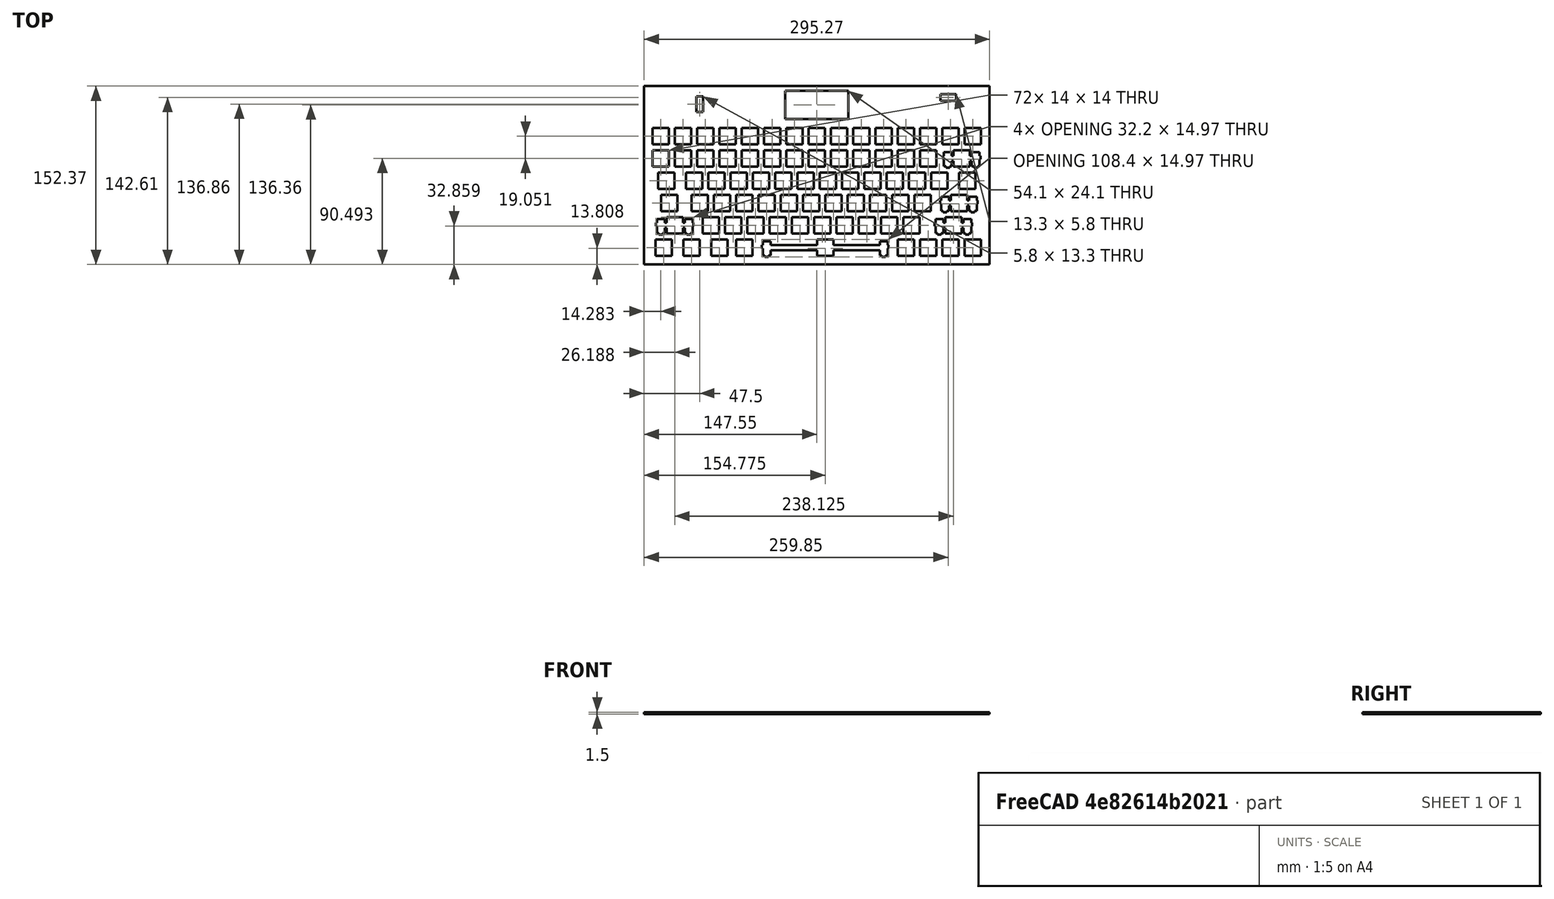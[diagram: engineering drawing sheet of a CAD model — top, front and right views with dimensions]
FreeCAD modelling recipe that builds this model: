
FCSTD DOCUMENT  (FreeCAD 0.21R33771 (Git))
Label: design
License: All rights reserved
LicenseURL: https://en.wikipedia.org/wiki/All_rights_reserved
objects: PartDesign::Body×2, Sketcher::SketchObject×1, PartDesign::Pad×1
note: 5 computed .brp shape members not serialized (recipe doc carries the construction recipe); baked Part::Feature solids carry a one-line shape summary decoded from their .brp

FEATURE [Sketcher::SketchObject] Sketch
  FullyConstrained = false
  MapMode = 5
  Support = -> [XY_Plane]
  sketch-geometry (484):
    g0: LineSegment StartX=55.0072 StartY=78.7329 StartZ=0 EndX=69.0079 EndY=78.7329 EndZ=0
    g1: LineSegment StartX=69.0079 StartY=78.7329 StartZ=0 EndX=69.0079 EndY=64.7333 EndZ=0
    g2: LineSegment StartX=69.0079 StartY=64.7333 StartZ=0 EndX=55.0072 EndY=64.7333 EndZ=0
    g3: LineSegment StartX=55.0072 StartY=64.7333 StartZ=0 EndX=55.0072 EndY=78.7329 EndZ=0
    g4: LineSegment StartX=64.5322 StartY=116.834 StartZ=0 EndX=78.5329 EndY=116.834 EndZ=0
    g5: LineSegment StartX=78.5329 StartY=116.834 StartZ=0 EndX=78.5329 EndY=102.835 EndZ=0
    g6: LineSegment StartX=78.5329 StartY=102.835 StartZ=0 EndX=64.5322 EndY=102.835 EndZ=0
    g7: LineSegment StartX=64.5322 StartY=102.835 StartZ=0 EndX=64.5322 EndY=116.834 EndZ=0
    g8: LineSegment StartX=0.0950846 StartY=152.658 StartZ=0 EndX=295.371 EndY=152.658 EndZ=0
    g9: LineSegment StartX=295.371 StartY=152.658 StartZ=0 EndX=295.371 EndY=0.2949 EndZ=0
    g10: LineSegment StartX=295.371 StartY=0.2949 StartZ=0 EndX=0.0950846 EndY=0.2949 EndZ=0
    g11: LineSegment StartX=0.0950846 StartY=0.2949 StartZ=0 EndX=0.0950846 EndY=152.658 EndZ=0
    g12: LineSegment StartX=147.876 StartY=21.5828 StartZ=0 EndX=147.876 EndY=16.8837 EndZ=0
    g13: LineSegment StartX=147.876 StartY=16.8837 StartZ=0 EndX=108.251 EndY=16.8837 EndZ=0
    g14: LineSegment StartX=108.251 StartY=16.8837 StartZ=0 EndX=108.251 EndY=20.1138 EndZ=0
    g15: LineSegment StartX=108.251 StartY=20.1138 StartZ=0 EndX=101.501 EndY=20.1138 EndZ=0
    g16: LineSegment StartX=101.501 StartY=20.1138 StartZ=0 EndX=101.501 EndY=16.8837 EndZ=0
    g17: LineSegment StartX=101.501 StartY=16.8837 StartZ=0 EndX=100.675 EndY=16.8837 EndZ=0
    g18: LineSegment StartX=100.675 StartY=16.8837 StartZ=0 EndX=100.675 EndY=14.0836 EndZ=0
    g19: LineSegment StartX=100.675 StartY=14.0836 StartZ=0 EndX=101.501 EndY=14.0836 EndZ=0
    g20: LineSegment StartX=101.501 StartY=14.0836 StartZ=0 EndX=101.501 EndY=7.81346 EndZ=0
    g21: LineSegment StartX=101.501 StartY=7.81346 StartZ=0 EndX=103.226 EndY=7.81346 EndZ=0
    g22: LineSegment StartX=103.226 StartY=7.81346 StartZ=0 EndX=103.226 EndY=6.61321 EndZ=0
    g23: LineSegment StartX=103.226 StartY=6.61321 StartZ=0 EndX=106.525 EndY=6.61321 EndZ=0
    g24: LineSegment StartX=106.525 StartY=6.61321 StartZ=0 EndX=106.525 EndY=7.81346 EndZ=0
    g25: LineSegment StartX=106.525 StartY=7.81346 StartZ=0 EndX=108.251 EndY=7.81346 EndZ=0
    g26: LineSegment StartX=108.251 StartY=7.81346 StartZ=0 EndX=108.251 EndY=12.2838 EndZ=0
    g27: LineSegment StartX=108.251 StartY=12.2838 StartZ=0 EndX=147.876 EndY=12.2838 EndZ=0
    g28: LineSegment StartX=147.876 StartY=12.2838 StartZ=0 EndX=147.876 EndY=7.58335 EndZ=0
    g29: LineSegment StartX=147.876 StartY=7.58335 StartZ=0 EndX=161.875 EndY=7.58335 EndZ=0
    g30: LineSegment StartX=161.875 StartY=7.58335 StartZ=0 EndX=161.875 EndY=12.2838 EndZ=0
    g31: LineSegment StartX=161.875 StartY=12.2838 StartZ=0 EndX=201.501 EndY=12.2838 EndZ=0
    g32: LineSegment StartX=201.501 StartY=12.2838 StartZ=0 EndX=201.501 EndY=7.81346 EndZ=0
    g33: LineSegment StartX=201.501 StartY=7.81346 StartZ=0 EndX=203.225 EndY=7.81346 EndZ=0
    g34: LineSegment StartX=203.225 StartY=7.81346 StartZ=0 EndX=203.225 EndY=6.61321 EndZ=0
    g35: LineSegment StartX=203.225 StartY=6.61321 StartZ=0 EndX=206.525 EndY=6.61321 EndZ=0
    g36: LineSegment StartX=206.525 StartY=6.61321 StartZ=0 EndX=206.525 EndY=7.81346 EndZ=0
    g37: LineSegment StartX=206.525 StartY=7.81346 StartZ=0 EndX=208.25 EndY=7.81346 EndZ=0
    g38: LineSegment StartX=208.25 StartY=7.81346 StartZ=0 EndX=208.25 EndY=14.0836 EndZ=0
    g39: LineSegment StartX=208.25 StartY=14.0836 StartZ=0 EndX=209.076 EndY=14.0836 EndZ=0
    g40: LineSegment StartX=209.076 StartY=14.0836 StartZ=0 EndX=209.076 EndY=16.8837 EndZ=0
    g41: LineSegment StartX=209.076 StartY=16.8837 StartZ=0 EndX=208.25 EndY=16.8837 EndZ=0
    g42: LineSegment StartX=208.25 StartY=16.8837 StartZ=0 EndX=208.25 EndY=20.1138 EndZ=0
    g43: LineSegment StartX=208.25 StartY=20.1138 StartZ=0 EndX=201.501 EndY=20.1138 EndZ=0
    g44: LineSegment StartX=201.501 StartY=20.1138 StartZ=0 EndX=201.501 EndY=16.8837 EndZ=0
    g45: LineSegment StartX=201.501 StartY=16.8837 StartZ=0 EndX=161.875 EndY=16.8837 EndZ=0
    g46: LineSegment StartX=161.875 StartY=16.8837 StartZ=0 EndX=161.875 EndY=21.5828 EndZ=0
    g47: LineSegment StartX=161.875 StartY=21.5828 StartZ=0 EndX=147.876 EndY=21.5828 EndZ=0
    g48: LineSegment StartX=9.76341 StartY=21.5828 StartZ=0 EndX=23.7629 EndY=21.5828 EndZ=0
    g49: LineSegment StartX=23.7629 StartY=21.5828 StartZ=0 EndX=23.7629 EndY=7.58335 EndZ=0
    g50: LineSegment StartX=23.7629 StartY=7.58335 StartZ=0 EndX=9.76341 EndY=7.58335 EndZ=0
    g51: LineSegment StartX=9.76341 StartY=7.58335 StartZ=0 EndX=9.76341 EndY=21.5828 EndZ=0
    g52: LineSegment StartX=33.5759 StartY=21.5828 StartZ=0 EndX=47.5753 EndY=21.5828 EndZ=0
    g53: LineSegment StartX=47.5753 StartY=21.5828 StartZ=0 EndX=47.5753 EndY=7.58335 EndZ=0
    g54: LineSegment StartX=47.5753 StartY=7.58335 StartZ=0 EndX=33.5759 EndY=7.58335 EndZ=0
    g55: LineSegment StartX=33.5759 StartY=7.58335 StartZ=0 EndX=33.5759 EndY=21.5828 EndZ=0
    g56: LineSegment StartX=57.3885 StartY=21.5828 StartZ=0 EndX=71.3878 EndY=21.5828 EndZ=0
    g57: LineSegment StartX=71.3878 StartY=21.5828 StartZ=0 EndX=71.3878 EndY=7.58335 EndZ=0
    g58: LineSegment StartX=71.3878 StartY=7.58335 StartZ=0 EndX=57.3885 EndY=7.58335 EndZ=0
    g59: LineSegment StartX=57.3885 StartY=7.58335 StartZ=0 EndX=57.3885 EndY=21.5828 EndZ=0
    g60: LineSegment StartX=78.8197 StartY=21.5828 StartZ=0 EndX=92.819 EndY=21.5828 EndZ=0
    g61: LineSegment StartX=92.819 StartY=21.5828 StartZ=0 EndX=92.819 EndY=7.58335 EndZ=0
    g62: LineSegment StartX=92.819 StartY=7.58335 StartZ=0 EndX=78.8197 EndY=7.58335 EndZ=0
    g63: LineSegment StartX=78.8197 StartY=7.58335 StartZ=0 EndX=78.8197 EndY=21.5828 EndZ=0
    g64: LineSegment StartX=216.932 StartY=21.5828 StartZ=0 EndX=230.933 EndY=21.5828 EndZ=0
    g65: LineSegment StartX=230.933 StartY=21.5828 StartZ=0 EndX=230.933 EndY=7.58335 EndZ=0
    g66: LineSegment StartX=230.933 StartY=7.58335 StartZ=0 EndX=216.932 EndY=7.58335 EndZ=0
    g67: LineSegment StartX=216.932 StartY=7.58335 StartZ=0 EndX=216.932 EndY=21.5828 EndZ=0
    g68: LineSegment StartX=235.982 StartY=21.5828 StartZ=0 EndX=249.983 EndY=21.5828 EndZ=0
    g69: LineSegment StartX=249.983 StartY=21.5828 StartZ=0 EndX=249.983 EndY=7.58335 EndZ=0
    g70: LineSegment StartX=249.983 StartY=7.58335 StartZ=0 EndX=235.982 EndY=7.58335 EndZ=0
    g71: LineSegment StartX=235.982 StartY=7.58335 StartZ=0 EndX=235.982 EndY=21.5828 EndZ=0
    g72: LineSegment StartX=255.032 StartY=21.5828 StartZ=0 EndX=269.033 EndY=21.5828 EndZ=0
    g73: LineSegment StartX=269.033 StartY=21.5828 StartZ=0 EndX=269.033 EndY=7.58335 EndZ=0
    g74: LineSegment StartX=269.033 StartY=7.58335 StartZ=0 EndX=255.032 EndY=7.58335 EndZ=0
    g75: LineSegment StartX=255.032 StartY=7.58335 StartZ=0 EndX=255.032 EndY=21.5828 EndZ=0
    g76: LineSegment StartX=274.082 StartY=21.5828 StartZ=0 EndX=288.083 EndY=21.5828 EndZ=0
    g77: LineSegment StartX=288.083 StartY=21.5828 StartZ=0 EndX=288.083 EndY=7.58335 EndZ=0
    g78: LineSegment StartX=288.083 StartY=7.58335 StartZ=0 EndX=274.082 EndY=7.58335 EndZ=0
    g79: LineSegment StartX=274.082 StartY=7.58335 StartZ=0 EndX=274.082 EndY=21.5828 EndZ=0
    g80: LineSegment StartX=19.2884 StartY=40.6344 StartZ=0 EndX=19.2884 EndY=35.9336 EndZ=0
    g81: LineSegment StartX=19.2884 StartY=35.9336 StartZ=0 EndX=17.7629 EndY=35.9336 EndZ=0
    g82: LineSegment StartX=17.7629 StartY=35.9336 StartZ=0 EndX=17.7629 EndY=39.164 EndZ=0
    g83: LineSegment StartX=17.7629 StartY=39.164 StartZ=0 EndX=11.0133 EndY=39.164 EndZ=0
    g84: LineSegment StartX=11.0133 StartY=39.164 StartZ=0 EndX=11.0133 EndY=35.9336 EndZ=0
    g85: LineSegment StartX=11.0133 StartY=35.9336 StartZ=0 EndX=10.1878 EndY=35.9336 EndZ=0
    g86: LineSegment StartX=10.1878 StartY=35.9336 StartZ=0 EndX=10.1878 EndY=33.1349 EndZ=0
    g87: LineSegment StartX=10.1878 StartY=33.1349 StartZ=0 EndX=11.0133 EndY=33.1349 EndZ=0
    g88: LineSegment StartX=11.0133 StartY=33.1349 StartZ=0 EndX=11.0133 EndY=26.8648 EndZ=0
    g89: LineSegment StartX=11.0133 StartY=26.8648 StartZ=0 EndX=12.7386 EndY=26.8648 EndZ=0
    g90: LineSegment StartX=12.7386 StartY=26.8648 StartZ=0 EndX=12.7386 EndY=25.6632 EndZ=0
    g91: LineSegment StartX=12.7386 StartY=25.6632 StartZ=0 EndX=16.039 EndY=25.6632 EndZ=0
    g92: LineSegment StartX=16.039 StartY=25.6632 StartZ=0 EndX=16.039 EndY=26.8648 EndZ=0
    g93: LineSegment StartX=16.039 StartY=26.8648 StartZ=0 EndX=17.7629 EndY=26.8648 EndZ=0
    g94: LineSegment StartX=17.7629 StartY=26.8648 StartZ=0 EndX=17.7629 EndY=31.3338 EndZ=0
    g95: LineSegment StartX=17.7629 StartY=31.3338 StartZ=0 EndX=19.2884 EndY=31.3338 EndZ=0
    g96: LineSegment StartX=19.2884 StartY=31.3338 StartZ=0 EndX=19.2884 EndY=26.6347 EndZ=0
    g97: LineSegment StartX=19.2884 StartY=26.6347 StartZ=0 EndX=33.2879 EndY=26.6347 EndZ=0
    g98: LineSegment StartX=33.2879 StartY=26.6347 StartZ=0 EndX=33.2879 EndY=31.3338 EndZ=0
    g99: LineSegment StartX=33.2879 StartY=31.3338 StartZ=0 EndX=34.8134 EndY=31.3338 EndZ=0
    g100: LineSegment StartX=34.8134 StartY=31.3338 StartZ=0 EndX=34.8134 EndY=26.8648 EndZ=0
    g101: LineSegment StartX=34.8134 StartY=26.8648 StartZ=0 EndX=36.5386 EndY=26.8648 EndZ=0
    g102: LineSegment StartX=36.5386 StartY=26.8648 StartZ=0 EndX=36.5386 EndY=25.6632 EndZ=0
    g103: LineSegment StartX=36.5386 StartY=25.6632 StartZ=0 EndX=39.8392 EndY=25.6632 EndZ=0
    g104: LineSegment StartX=39.8392 StartY=25.6632 StartZ=0 EndX=39.8392 EndY=26.8648 EndZ=0
    g105: LineSegment StartX=39.8392 StartY=26.8648 StartZ=0 EndX=41.5629 EndY=26.8648 EndZ=0
    g106: LineSegment StartX=41.5629 StartY=26.8648 StartZ=0 EndX=41.5629 EndY=33.1349 EndZ=0
    g107: LineSegment StartX=41.5629 StartY=33.1349 StartZ=0 EndX=42.3884 EndY=33.1349 EndZ=0
    g108: LineSegment StartX=42.3884 StartY=33.1349 StartZ=0 EndX=42.3884 EndY=35.9336 EndZ=0
    g109: LineSegment StartX=42.3884 StartY=35.9336 StartZ=0 EndX=41.5629 EndY=35.9336 EndZ=0
    g110: LineSegment StartX=41.5629 StartY=35.9336 StartZ=0 EndX=41.5629 EndY=39.164 EndZ=0
    g111: LineSegment StartX=41.5629 StartY=39.164 StartZ=0 EndX=34.8134 EndY=39.164 EndZ=0
    g112: LineSegment StartX=34.8134 StartY=39.164 StartZ=0 EndX=34.8134 EndY=35.9336 EndZ=0
    g113: LineSegment StartX=34.8134 StartY=35.9336 StartZ=0 EndX=33.2879 EndY=35.9336 EndZ=0
    g114: LineSegment StartX=33.2879 StartY=35.9336 StartZ=0 EndX=33.2879 EndY=40.6344 EndZ=0
    g115: LineSegment StartX=33.2879 StartY=40.6344 StartZ=0 EndX=19.2884 EndY=40.6344 EndZ=0
    g116: LineSegment StartX=257.413 StartY=40.6344 StartZ=0 EndX=257.413 EndY=35.9336 EndZ=0
    g117: LineSegment StartX=257.413 StartY=35.9336 StartZ=0 EndX=255.888 EndY=35.9336 EndZ=0
    g118: LineSegment StartX=255.888 StartY=35.9336 StartZ=0 EndX=255.888 EndY=39.164 EndZ=0
    g119: LineSegment StartX=255.888 StartY=39.164 StartZ=0 EndX=249.138 EndY=39.164 EndZ=0
    g120: LineSegment StartX=249.138 StartY=39.164 StartZ=0 EndX=249.138 EndY=35.9336 EndZ=0
    g121: LineSegment StartX=249.138 StartY=35.9336 StartZ=0 EndX=248.313 EndY=35.9336 EndZ=0
    g122: LineSegment StartX=248.313 StartY=35.9336 StartZ=0 EndX=248.313 EndY=33.1349 EndZ=0
    g123: LineSegment StartX=248.313 StartY=33.1349 StartZ=0 EndX=249.138 EndY=33.1349 EndZ=0
    g124: LineSegment StartX=249.138 StartY=33.1349 StartZ=0 EndX=249.138 EndY=26.8648 EndZ=0
    g125: LineSegment StartX=249.138 StartY=26.8648 StartZ=0 EndX=250.863 EndY=26.8648 EndZ=0
    g126: LineSegment StartX=250.863 StartY=26.8648 StartZ=0 EndX=250.863 EndY=25.6632 EndZ=0
    g127: LineSegment StartX=250.863 StartY=25.6632 StartZ=0 EndX=254.164 EndY=25.6632 EndZ=0
    g128: LineSegment StartX=254.164 StartY=25.6632 StartZ=0 EndX=254.164 EndY=26.8648 EndZ=0
    g129: LineSegment StartX=254.164 StartY=26.8648 StartZ=0 EndX=255.888 EndY=26.8648 EndZ=0
    g130: LineSegment StartX=255.888 StartY=26.8648 StartZ=0 EndX=255.888 EndY=31.3338 EndZ=0
    g131: LineSegment StartX=255.888 StartY=31.3338 StartZ=0 EndX=257.413 EndY=31.3338 EndZ=0
    g132: LineSegment StartX=257.413 StartY=31.3338 StartZ=0 EndX=257.413 EndY=26.6347 EndZ=0
    g133: LineSegment StartX=257.413 StartY=26.6347 StartZ=0 EndX=271.413 EndY=26.6347 EndZ=0
    g134: LineSegment StartX=271.413 StartY=26.6347 StartZ=0 EndX=271.413 EndY=31.3338 EndZ=0
    g135: LineSegment StartX=271.413 StartY=31.3338 StartZ=0 EndX=272.939 EndY=31.3338 EndZ=0
    g136: LineSegment StartX=272.939 StartY=31.3338 StartZ=0 EndX=272.939 EndY=26.8648 EndZ=0
    g137: LineSegment StartX=272.939 StartY=26.8648 StartZ=0 EndX=274.664 EndY=26.8648 EndZ=0
    g138: LineSegment StartX=274.664 StartY=26.8648 StartZ=0 EndX=274.664 EndY=25.6632 EndZ=0
    g139: LineSegment StartX=274.664 StartY=25.6632 StartZ=0 EndX=277.964 EndY=25.6632 EndZ=0
    g140: LineSegment StartX=277.964 StartY=25.6632 StartZ=0 EndX=277.964 EndY=26.8648 EndZ=0
    g141: LineSegment StartX=277.964 StartY=26.8648 StartZ=0 EndX=279.688 EndY=26.8648 EndZ=0
    g142: LineSegment StartX=279.688 StartY=26.8648 StartZ=0 EndX=279.688 EndY=33.1349 EndZ=0
    g143: LineSegment StartX=279.688 StartY=33.1349 StartZ=0 EndX=280.513 EndY=33.1349 EndZ=0
    g144: LineSegment StartX=280.513 StartY=33.1349 StartZ=0 EndX=280.513 EndY=35.9336 EndZ=0
    g145: LineSegment StartX=280.513 StartY=35.9336 StartZ=0 EndX=279.688 EndY=35.9336 EndZ=0
    g146: LineSegment StartX=279.688 StartY=35.9336 StartZ=0 EndX=279.688 EndY=39.164 EndZ=0
    g147: LineSegment StartX=279.688 StartY=39.164 StartZ=0 EndX=272.939 EndY=39.164 EndZ=0
    g148: LineSegment StartX=272.939 StartY=39.164 StartZ=0 EndX=272.939 EndY=35.9336 EndZ=0
    g149: LineSegment StartX=272.939 StartY=35.9336 StartZ=0 EndX=271.413 EndY=35.9336 EndZ=0
    g150: LineSegment StartX=271.413 StartY=35.9336 StartZ=0 EndX=271.413 EndY=40.6344 EndZ=0
    g151: LineSegment StartX=271.413 StartY=40.6344 StartZ=0 EndX=257.413 EndY=40.6344 EndZ=0
    g152: LineSegment StartX=50.2447 StartY=40.6344 StartZ=0 EndX=64.244 EndY=40.6344 EndZ=0
    g153: LineSegment StartX=64.244 StartY=40.6344 StartZ=0 EndX=64.244 EndY=26.6347 EndZ=0
    g154: LineSegment StartX=64.244 StartY=26.6347 StartZ=0 EndX=50.2447 EndY=26.6347 EndZ=0
    g155: LineSegment StartX=50.2447 StartY=26.6347 StartZ=0 EndX=50.2447 EndY=40.6344 EndZ=0
    g156: LineSegment StartX=69.2947 StartY=40.6344 StartZ=0 EndX=83.294 EndY=40.6344 EndZ=0
    g157: LineSegment StartX=83.294 StartY=40.6344 StartZ=0 EndX=83.294 EndY=26.6347 EndZ=0
    g158: LineSegment StartX=83.294 StartY=26.6347 StartZ=0 EndX=69.2947 EndY=26.6347 EndZ=0
    g159: LineSegment StartX=69.2947 StartY=26.6347 StartZ=0 EndX=69.2947 EndY=40.6344 EndZ=0
    g160: LineSegment StartX=88.3447 StartY=40.6344 StartZ=0 EndX=102.344 EndY=40.6344 EndZ=0
    g161: LineSegment StartX=102.344 StartY=40.6344 StartZ=0 EndX=102.344 EndY=26.6347 EndZ=0
    g162: LineSegment StartX=102.344 StartY=26.6347 StartZ=0 EndX=88.3447 EndY=26.6347 EndZ=0
    g163: LineSegment StartX=88.3447 StartY=26.6347 StartZ=0 EndX=88.3447 EndY=40.6344 EndZ=0
    g164: LineSegment StartX=107.395 StartY=40.6344 StartZ=0 EndX=121.394 EndY=40.6344 EndZ=0
    g165: LineSegment StartX=121.394 StartY=40.6344 StartZ=0 EndX=121.394 EndY=26.6347 EndZ=0
    g166: LineSegment StartX=121.394 StartY=26.6347 StartZ=0 EndX=107.395 EndY=26.6347 EndZ=0
    g167: LineSegment StartX=107.395 StartY=26.6347 StartZ=0 EndX=107.395 EndY=40.6344 EndZ=0
    g168: LineSegment StartX=126.445 StartY=40.6344 StartZ=0 EndX=140.444 EndY=40.6344 EndZ=0
    g169: LineSegment StartX=140.444 StartY=40.6344 StartZ=0 EndX=140.444 EndY=26.6347 EndZ=0
    g170: LineSegment StartX=140.444 StartY=26.6347 StartZ=0 EndX=126.445 EndY=26.6347 EndZ=0
    g171: LineSegment StartX=126.445 StartY=26.6347 StartZ=0 EndX=126.445 EndY=40.6344 EndZ=0
    g172: LineSegment StartX=145.495 StartY=40.6344 StartZ=0 EndX=159.494 EndY=40.6344 EndZ=0
    g173: LineSegment StartX=159.494 StartY=40.6344 StartZ=0 EndX=159.494 EndY=26.6347 EndZ=0
    g174: LineSegment StartX=159.494 StartY=26.6347 StartZ=0 EndX=145.495 EndY=26.6347 EndZ=0
    g175: LineSegment StartX=145.495 StartY=26.6347 StartZ=0 EndX=145.495 EndY=40.6344 EndZ=0
    g176: LineSegment StartX=164.545 StartY=40.6344 StartZ=0 EndX=178.544 EndY=40.6344 EndZ=0
    g177: LineSegment StartX=178.544 StartY=40.6344 StartZ=0 EndX=178.544 EndY=26.6347 EndZ=0
    g178: LineSegment StartX=178.544 StartY=26.6347 StartZ=0 EndX=164.545 EndY=26.6347 EndZ=0
    g179: LineSegment StartX=164.545 StartY=26.6347 StartZ=0 EndX=164.545 EndY=40.6344 EndZ=0
    g180: LineSegment StartX=183.595 StartY=40.6344 StartZ=0 EndX=197.594 EndY=40.6344 EndZ=0
    g181: LineSegment StartX=197.594 StartY=40.6344 StartZ=0 EndX=197.594 EndY=26.6347 EndZ=0
    g182: LineSegment StartX=197.594 StartY=26.6347 StartZ=0 EndX=183.595 EndY=26.6347 EndZ=0
    g183: LineSegment StartX=183.595 StartY=26.6347 StartZ=0 EndX=183.595 EndY=40.6344 EndZ=0
    g184: LineSegment StartX=202.645 StartY=40.6344 StartZ=0 EndX=216.644 EndY=40.6344 EndZ=0
    g185: LineSegment StartX=216.644 StartY=40.6344 StartZ=0 EndX=216.644 EndY=26.6347 EndZ=0
    g186: LineSegment StartX=216.644 StartY=26.6347 StartZ=0 EndX=202.645 EndY=26.6347 EndZ=0
    g187: LineSegment StartX=202.645 StartY=26.6347 StartZ=0 EndX=202.645 EndY=40.6344 EndZ=0
    g188: LineSegment StartX=221.695 StartY=40.6344 StartZ=0 EndX=235.694 EndY=40.6344 EndZ=0
    g189: LineSegment StartX=235.694 StartY=40.6344 StartZ=0 EndX=235.694 EndY=26.6347 EndZ=0
    g190: LineSegment StartX=235.694 StartY=26.6347 StartZ=0 EndX=221.695 EndY=26.6347 EndZ=0
    g191: LineSegment StartX=221.695 StartY=26.6347 StartZ=0 EndX=221.695 EndY=40.6344 EndZ=0
    g192: LineSegment StartX=262.176 StartY=59.6829 StartZ=0 EndX=262.176 EndY=54.9836 EndZ=0
    g193: LineSegment StartX=262.176 StartY=54.9836 StartZ=0 EndX=260.651 EndY=54.9836 EndZ=0
    g194: LineSegment StartX=260.651 StartY=54.9836 StartZ=0 EndX=260.651 EndY=58.214 EndZ=0
    g195: LineSegment StartX=260.651 StartY=58.214 StartZ=0 EndX=253.899 EndY=58.214 EndZ=0
    g196: LineSegment StartX=253.899 StartY=58.214 StartZ=0 EndX=253.899 EndY=54.9836 EndZ=0
    g197: LineSegment StartX=253.899 StartY=54.9836 StartZ=0 EndX=253.075 EndY=54.9836 EndZ=0
    g198: LineSegment StartX=253.075 StartY=54.9836 StartZ=0 EndX=253.075 EndY=52.1836 EndZ=0
    g199: LineSegment StartX=253.075 StartY=52.1836 StartZ=0 EndX=253.899 EndY=52.1836 EndZ=0
    g200: LineSegment StartX=253.899 StartY=52.1836 StartZ=0 EndX=253.899 EndY=45.9147 EndZ=0
    g201: LineSegment StartX=253.899 StartY=45.9147 StartZ=0 EndX=255.626 EndY=45.9147 EndZ=0
    g202: LineSegment StartX=255.626 StartY=45.9147 StartZ=0 EndX=255.626 EndY=44.7132 EndZ=0
    g203: LineSegment StartX=255.626 StartY=44.7132 StartZ=0 EndX=258.925 EndY=44.7132 EndZ=0
    g204: LineSegment StartX=258.925 StartY=44.7132 StartZ=0 EndX=258.925 EndY=45.9147 EndZ=0
    g205: LineSegment StartX=258.925 StartY=45.9147 StartZ=0 EndX=260.651 EndY=45.9147 EndZ=0
    g206: LineSegment StartX=260.651 StartY=45.9147 StartZ=0 EndX=260.651 EndY=50.3837 EndZ=0
    g207: LineSegment StartX=260.651 StartY=50.3837 StartZ=0 EndX=262.176 EndY=50.3837 EndZ=0
    g208: LineSegment StartX=262.176 StartY=50.3837 StartZ=0 EndX=262.176 EndY=45.6833 EndZ=0
    g209: LineSegment StartX=262.176 StartY=45.6833 StartZ=0 EndX=276.175 EndY=45.6833 EndZ=0
    g210: LineSegment StartX=276.175 StartY=45.6833 StartZ=0 EndX=276.175 EndY=50.3837 EndZ=0
    g211: LineSegment StartX=276.175 StartY=50.3837 StartZ=0 EndX=277.701 EndY=50.3837 EndZ=0
    g212: LineSegment StartX=277.701 StartY=50.3837 StartZ=0 EndX=277.701 EndY=45.9147 EndZ=0
    g213: LineSegment StartX=277.701 StartY=45.9147 StartZ=0 EndX=279.425 EndY=45.9147 EndZ=0
    g214: LineSegment StartX=279.425 StartY=45.9147 StartZ=0 EndX=279.425 EndY=44.7132 EndZ=0
    g215: LineSegment StartX=279.425 StartY=44.7132 StartZ=0 EndX=282.725 EndY=44.7132 EndZ=0
    g216: LineSegment StartX=282.725 StartY=44.7132 StartZ=0 EndX=282.725 EndY=45.9147 EndZ=0
    g217: LineSegment StartX=282.725 StartY=45.9147 StartZ=0 EndX=284.45 EndY=45.9147 EndZ=0
    g218: LineSegment StartX=284.45 StartY=45.9147 StartZ=0 EndX=284.45 EndY=52.1836 EndZ=0
    g219: LineSegment StartX=284.45 StartY=52.1836 StartZ=0 EndX=285.276 EndY=52.1836 EndZ=0
    g220: LineSegment StartX=285.276 StartY=52.1836 StartZ=0 EndX=285.276 EndY=54.9836 EndZ=0
    g221: LineSegment StartX=285.276 StartY=54.9836 StartZ=0 EndX=284.45 EndY=54.9836 EndZ=0
    g222: LineSegment StartX=284.45 StartY=54.9836 StartZ=0 EndX=284.45 EndY=58.214 EndZ=0
    g223: LineSegment StartX=284.45 StartY=58.214 StartZ=0 EndX=277.701 EndY=58.214 EndZ=0
    g224: LineSegment StartX=277.701 StartY=58.214 StartZ=0 EndX=277.701 EndY=54.9836 EndZ=0
    g225: LineSegment StartX=277.701 StartY=54.9836 StartZ=0 EndX=276.175 EndY=54.9836 EndZ=0
    g226: LineSegment StartX=276.175 StartY=54.9836 StartZ=0 EndX=276.175 EndY=59.6829 EndZ=0
    g227: LineSegment StartX=276.175 StartY=59.6829 StartZ=0 EndX=262.176 EndY=59.6829 EndZ=0
    g228: LineSegment StartX=14.5259 StartY=59.6829 StartZ=0 EndX=28.5254 EndY=59.6829 EndZ=0
    g229: LineSegment StartX=28.5254 StartY=59.6829 StartZ=0 EndX=28.5254 EndY=45.6833 EndZ=0
    g230: LineSegment StartX=28.5254 StartY=45.6833 StartZ=0 EndX=14.5259 EndY=45.6833 EndZ=0
    g231: LineSegment StartX=14.5259 StartY=45.6833 StartZ=0 EndX=14.5259 EndY=59.6829 EndZ=0
    g232: LineSegment StartX=40.7197 StartY=59.6829 StartZ=0 EndX=54.719 EndY=59.6829 EndZ=0
    g233: LineSegment StartX=54.719 StartY=59.6829 StartZ=0 EndX=54.719 EndY=45.6833 EndZ=0
    g234: LineSegment StartX=54.719 StartY=45.6833 StartZ=0 EndX=40.7197 EndY=45.6833 EndZ=0
    g235: LineSegment StartX=40.7197 StartY=45.6833 StartZ=0 EndX=40.7197 EndY=59.6829 EndZ=0
    g236: LineSegment StartX=59.7697 StartY=59.6829 StartZ=0 EndX=73.769 EndY=59.6829 EndZ=0
    g237: LineSegment StartX=73.769 StartY=59.6829 StartZ=0 EndX=73.769 EndY=45.6833 EndZ=0
    g238: LineSegment StartX=73.769 StartY=45.6833 StartZ=0 EndX=59.7697 EndY=45.6833 EndZ=0
    g239: LineSegment StartX=59.7697 StartY=45.6833 StartZ=0 EndX=59.7697 EndY=59.6829 EndZ=0
    g240: LineSegment StartX=78.8197 StartY=59.6829 StartZ=0 EndX=92.819 EndY=59.6829 EndZ=0
    g241: LineSegment StartX=92.819 StartY=59.6829 StartZ=0 EndX=92.819 EndY=45.6833 EndZ=0
    g242: LineSegment StartX=92.819 StartY=45.6833 StartZ=0 EndX=78.8197 EndY=45.6833 EndZ=0
    g243: LineSegment StartX=78.8197 StartY=45.6833 StartZ=0 EndX=78.8197 EndY=59.6829 EndZ=0
    g244: LineSegment StartX=97.8697 StartY=59.6829 StartZ=0 EndX=111.869 EndY=59.6829 EndZ=0
    g245: LineSegment StartX=111.869 StartY=59.6829 StartZ=0 EndX=111.869 EndY=45.6833 EndZ=0
    g246: LineSegment StartX=111.869 StartY=45.6833 StartZ=0 EndX=97.8697 EndY=45.6833 EndZ=0
    g247: LineSegment StartX=97.8697 StartY=45.6833 StartZ=0 EndX=97.8697 EndY=59.6829 EndZ=0
    g248: LineSegment StartX=116.92 StartY=59.6829 StartZ=0 EndX=130.919 EndY=59.6829 EndZ=0
    g249: LineSegment StartX=130.919 StartY=59.6829 StartZ=0 EndX=130.919 EndY=45.6833 EndZ=0
    g250: LineSegment StartX=130.919 StartY=45.6833 StartZ=0 EndX=116.92 EndY=45.6833 EndZ=0
    g251: LineSegment StartX=116.92 StartY=45.6833 StartZ=0 EndX=116.92 EndY=59.6829 EndZ=0
    g252: LineSegment StartX=135.97 StartY=59.6829 StartZ=0 EndX=149.969 EndY=59.6829 EndZ=0
    g253: LineSegment StartX=149.969 StartY=59.6829 StartZ=0 EndX=149.969 EndY=45.6833 EndZ=0
    g254: LineSegment StartX=149.969 StartY=45.6833 StartZ=0 EndX=135.97 EndY=45.6833 EndZ=0
    g255: LineSegment StartX=135.97 StartY=45.6833 StartZ=0 EndX=135.97 EndY=59.6829 EndZ=0
    g256: LineSegment StartX=155.02 StartY=59.6829 StartZ=0 EndX=169.019 EndY=59.6829 EndZ=0
    g257: LineSegment StartX=169.019 StartY=59.6829 StartZ=0 EndX=169.019 EndY=45.6833 EndZ=0
    g258: LineSegment StartX=169.019 StartY=45.6833 StartZ=0 EndX=155.02 EndY=45.6833 EndZ=0
    g259: LineSegment StartX=155.02 StartY=45.6833 StartZ=0 EndX=155.02 EndY=59.6829 EndZ=0
    g260: LineSegment StartX=174.07 StartY=59.6829 StartZ=0 EndX=188.069 EndY=59.6829 EndZ=0
    g261: LineSegment StartX=188.069 StartY=59.6829 StartZ=0 EndX=188.069 EndY=45.6833 EndZ=0
    g262: LineSegment StartX=188.069 StartY=45.6833 StartZ=0 EndX=174.07 EndY=45.6833 EndZ=0
    g263: LineSegment StartX=174.07 StartY=45.6833 StartZ=0 EndX=174.07 EndY=59.6829 EndZ=0
    g264: LineSegment StartX=193.12 StartY=59.6829 StartZ=0 EndX=207.119 EndY=59.6829 EndZ=0
    g265: LineSegment StartX=207.119 StartY=59.6829 StartZ=0 EndX=207.119 EndY=45.6833 EndZ=0
    g266: LineSegment StartX=207.119 StartY=45.6833 StartZ=0 EndX=193.12 EndY=45.6833 EndZ=0
    g267: LineSegment StartX=193.12 StartY=45.6833 StartZ=0 EndX=193.12 EndY=59.6829 EndZ=0
    g268: LineSegment StartX=212.17 StartY=59.6829 StartZ=0 EndX=226.169 EndY=59.6829 EndZ=0
    g269: LineSegment StartX=226.169 StartY=59.6829 StartZ=0 EndX=226.169 EndY=45.6833 EndZ=0
    g270: LineSegment StartX=226.169 StartY=45.6833 StartZ=0 EndX=212.17 EndY=45.6833 EndZ=0
    g271: LineSegment StartX=212.17 StartY=45.6833 StartZ=0 EndX=212.17 EndY=59.6829 EndZ=0
    g272: LineSegment StartX=231.22 StartY=59.6829 StartZ=0 EndX=245.219 EndY=59.6829 EndZ=0
    g273: LineSegment StartX=245.219 StartY=59.6829 StartZ=0 EndX=245.219 EndY=45.6833 EndZ=0
    g274: LineSegment StartX=245.219 StartY=45.6833 StartZ=0 EndX=231.22 EndY=45.6833 EndZ=0
    g275: LineSegment StartX=231.22 StartY=45.6833 StartZ=0 EndX=231.22 EndY=59.6829 EndZ=0
    g276: LineSegment StartX=12.1447 StartY=78.7329 StartZ=0 EndX=26.1441 EndY=78.7329 EndZ=0
    g277: LineSegment StartX=26.1441 StartY=78.7329 StartZ=0 EndX=26.1441 EndY=64.7333 EndZ=0
    g278: LineSegment StartX=26.1441 StartY=64.7333 StartZ=0 EndX=12.1447 EndY=64.7333 EndZ=0
    g279: LineSegment StartX=12.1447 StartY=64.7333 StartZ=0 EndX=12.1447 EndY=78.7329 EndZ=0
    g280: LineSegment StartX=35.9572 StartY=78.7329 StartZ=0 EndX=49.9579 EndY=78.7329 EndZ=0
    g281: LineSegment StartX=49.9579 StartY=78.7329 StartZ=0 EndX=49.9579 EndY=64.7333 EndZ=0
    g282: LineSegment StartX=49.9579 StartY=64.7333 StartZ=0 EndX=35.9572 EndY=64.7333 EndZ=0
    g283: LineSegment StartX=35.9572 StartY=64.7333 StartZ=0 EndX=35.9572 EndY=78.7329 EndZ=0
    g284: LineSegment StartX=74.0572 StartY=78.7329 StartZ=0 EndX=88.0579 EndY=78.7329 EndZ=0
    g285: LineSegment StartX=88.0579 StartY=78.7329 StartZ=0 EndX=88.0579 EndY=64.7333 EndZ=0
    g286: LineSegment StartX=88.0579 StartY=64.7333 StartZ=0 EndX=74.0572 EndY=64.7333 EndZ=0
    g287: LineSegment StartX=74.0572 StartY=64.7333 StartZ=0 EndX=74.0572 EndY=78.7329 EndZ=0
    g288: LineSegment StartX=93.1072 StartY=78.7329 StartZ=0 EndX=107.107 EndY=78.7329 EndZ=0
    g289: LineSegment StartX=107.107 StartY=78.7329 StartZ=0 EndX=107.107 EndY=64.7333 EndZ=0
    g290: LineSegment StartX=107.107 StartY=64.7333 StartZ=0 EndX=93.1072 EndY=64.7333 EndZ=0
    g291: LineSegment StartX=93.1072 StartY=64.7333 StartZ=0 EndX=93.1072 EndY=78.7329 EndZ=0
    g292: LineSegment StartX=112.157 StartY=78.7329 StartZ=0 EndX=126.157 EndY=78.7329 EndZ=0
    g293: LineSegment StartX=126.157 StartY=78.7329 StartZ=0 EndX=126.157 EndY=64.7333 EndZ=0
    g294: LineSegment StartX=126.157 StartY=64.7333 StartZ=0 EndX=112.157 EndY=64.7333 EndZ=0
    g295: LineSegment StartX=112.157 StartY=64.7333 StartZ=0 EndX=112.157 EndY=78.7329 EndZ=0
    g296: LineSegment StartX=131.207 StartY=78.7329 StartZ=0 EndX=145.208 EndY=78.7329 EndZ=0
    g297: LineSegment StartX=145.208 StartY=78.7329 StartZ=0 EndX=145.208 EndY=64.7333 EndZ=0
    g298: LineSegment StartX=145.208 StartY=64.7333 StartZ=0 EndX=131.207 EndY=64.7333 EndZ=0
    g299: LineSegment StartX=131.207 StartY=64.7333 StartZ=0 EndX=131.207 EndY=78.7329 EndZ=0
    g300: LineSegment StartX=150.257 StartY=78.7329 StartZ=0 EndX=164.258 EndY=78.7329 EndZ=0
    g301: LineSegment StartX=164.258 StartY=78.7329 StartZ=0 EndX=164.258 EndY=64.7333 EndZ=0
    g302: LineSegment StartX=164.258 StartY=64.7333 StartZ=0 EndX=150.257 EndY=64.7333 EndZ=0
    g303: LineSegment StartX=150.257 StartY=64.7333 StartZ=0 EndX=150.257 EndY=78.7329 EndZ=0
    g304: LineSegment StartX=169.307 StartY=78.7329 StartZ=0 EndX=183.308 EndY=78.7329 EndZ=0
    g305: LineSegment StartX=183.308 StartY=78.7329 StartZ=0 EndX=183.308 EndY=64.7333 EndZ=0
    g306: LineSegment StartX=183.308 StartY=64.7333 StartZ=0 EndX=169.307 EndY=64.7333 EndZ=0
    g307: LineSegment StartX=169.307 StartY=64.7333 StartZ=0 EndX=169.307 EndY=78.7329 EndZ=0
    g308: LineSegment StartX=188.357 StartY=78.7329 StartZ=0 EndX=202.358 EndY=78.7329 EndZ=0
    g309: LineSegment StartX=202.358 StartY=78.7329 StartZ=0 EndX=202.358 EndY=64.7333 EndZ=0
    g310: LineSegment StartX=202.358 StartY=64.7333 StartZ=0 EndX=188.357 EndY=64.7333 EndZ=0
    g311: LineSegment StartX=188.357 StartY=64.7333 StartZ=0 EndX=188.357 EndY=78.7329 EndZ=0
    g312: LineSegment StartX=207.407 StartY=78.7329 StartZ=0 EndX=221.408 EndY=78.7329 EndZ=0
    g313: LineSegment StartX=221.408 StartY=78.7329 StartZ=0 EndX=221.408 EndY=64.7333 EndZ=0
    g314: LineSegment StartX=221.408 StartY=64.7333 StartZ=0 EndX=207.407 EndY=64.7333 EndZ=0
    g315: LineSegment StartX=207.407 StartY=64.7333 StartZ=0 EndX=207.407 EndY=78.7329 EndZ=0
    g316: LineSegment StartX=226.457 StartY=78.7329 StartZ=0 EndX=240.458 EndY=78.7329 EndZ=0
    g317: LineSegment StartX=240.458 StartY=78.7329 StartZ=0 EndX=240.458 EndY=64.7333 EndZ=0
    g318: LineSegment StartX=240.458 StartY=64.7333 StartZ=0 EndX=226.457 EndY=64.7333 EndZ=0
    g319: LineSegment StartX=226.457 StartY=64.7333 StartZ=0 EndX=226.457 EndY=78.7329 EndZ=0
    g320: LineSegment StartX=245.507 StartY=78.7329 StartZ=0 EndX=259.508 EndY=78.7329 EndZ=0
    g321: LineSegment StartX=259.508 StartY=78.7329 StartZ=0 EndX=259.508 EndY=64.7333 EndZ=0
    g322: LineSegment StartX=259.508 StartY=64.7333 StartZ=0 EndX=245.507 EndY=64.7333 EndZ=0
    g323: LineSegment StartX=245.507 StartY=64.7333 StartZ=0 EndX=245.507 EndY=78.7329 EndZ=0
    g324: LineSegment StartX=269.32 StartY=78.7329 StartZ=0 EndX=283.319 EndY=78.7329 EndZ=0
    g325: LineSegment StartX=283.319 StartY=78.7329 StartZ=0 EndX=283.319 EndY=64.7333 EndZ=0
    g326: LineSegment StartX=283.319 StartY=64.7333 StartZ=0 EndX=269.32 EndY=64.7333 EndZ=0
    g327: LineSegment StartX=269.32 StartY=64.7333 StartZ=0 EndX=269.32 EndY=78.7329 EndZ=0
    g328: LineSegment StartX=264.557 StartY=97.7829 StartZ=0 EndX=264.557 EndY=93.0836 EndZ=0
    g329: LineSegment StartX=264.557 StartY=93.0836 StartZ=0 EndX=263.033 EndY=93.0836 EndZ=0
    g330: LineSegment StartX=263.033 StartY=93.0836 StartZ=0 EndX=263.033 EndY=96.314 EndZ=0
    g331: LineSegment StartX=263.033 StartY=96.314 StartZ=0 EndX=256.282 EndY=96.314 EndZ=0
    g332: LineSegment StartX=256.282 StartY=96.314 StartZ=0 EndX=256.282 EndY=93.0836 EndZ=0
    g333: LineSegment StartX=256.282 StartY=93.0836 StartZ=0 EndX=255.458 EndY=93.0836 EndZ=0
    g334: LineSegment StartX=255.458 StartY=93.0836 StartZ=0 EndX=255.458 EndY=90.2836 EndZ=0
    g335: LineSegment StartX=255.458 StartY=90.2836 StartZ=0 EndX=256.282 EndY=90.2836 EndZ=0
    g336: LineSegment StartX=256.282 StartY=90.2836 StartZ=0 EndX=256.282 EndY=84.0133 EndZ=0
    g337: LineSegment StartX=256.282 StartY=84.0133 StartZ=0 EndX=258.007 EndY=84.0133 EndZ=0
    g338: LineSegment StartX=258.007 StartY=84.0133 StartZ=0 EndX=258.007 EndY=82.8132 EndZ=0
    g339: LineSegment StartX=258.007 StartY=82.8132 StartZ=0 EndX=261.308 EndY=82.8132 EndZ=0
    g340: LineSegment StartX=261.308 StartY=82.8132 StartZ=0 EndX=261.308 EndY=84.0133 EndZ=0
    g341: LineSegment StartX=261.308 StartY=84.0133 StartZ=0 EndX=263.033 EndY=84.0133 EndZ=0
    g342: LineSegment StartX=263.033 StartY=84.0133 StartZ=0 EndX=263.033 EndY=88.4837 EndZ=0
    g343: LineSegment StartX=263.033 StartY=88.4837 StartZ=0 EndX=264.557 EndY=88.4837 EndZ=0
    g344: LineSegment StartX=264.557 StartY=88.4837 StartZ=0 EndX=264.557 EndY=83.7833 EndZ=0
    g345: LineSegment StartX=264.557 StartY=83.7833 StartZ=0 EndX=278.558 EndY=83.7833 EndZ=0
    g346: LineSegment StartX=278.558 StartY=83.7833 StartZ=0 EndX=278.558 EndY=88.4837 EndZ=0
    g347: LineSegment StartX=278.558 StartY=88.4837 StartZ=0 EndX=280.082 EndY=88.4837 EndZ=0
    g348: LineSegment StartX=280.082 StartY=88.4837 StartZ=0 EndX=280.082 EndY=84.0133 EndZ=0
    g349: LineSegment StartX=280.082 StartY=84.0133 StartZ=0 EndX=281.807 EndY=84.0133 EndZ=0
    g350: LineSegment StartX=281.807 StartY=84.0133 StartZ=0 EndX=281.807 EndY=82.8132 EndZ=0
    g351: LineSegment StartX=281.807 StartY=82.8132 StartZ=0 EndX=285.108 EndY=82.8132 EndZ=0
    g352: LineSegment StartX=285.108 StartY=82.8132 StartZ=0 EndX=285.108 EndY=84.0133 EndZ=0
    g353: LineSegment StartX=285.108 StartY=84.0133 StartZ=0 EndX=286.833 EndY=84.0133 EndZ=0
    g354: LineSegment StartX=286.833 StartY=84.0133 StartZ=0 EndX=286.833 EndY=90.2836 EndZ=0
    g355: LineSegment StartX=286.833 StartY=90.2836 StartZ=0 EndX=287.657 EndY=90.2836 EndZ=0
    g356: LineSegment StartX=287.657 StartY=90.2836 StartZ=0 EndX=287.657 EndY=93.0836 EndZ=0
    g357: LineSegment StartX=287.657 StartY=93.0836 StartZ=0 EndX=286.833 EndY=93.0836 EndZ=0
    g358: LineSegment StartX=286.833 StartY=93.0836 StartZ=0 EndX=286.833 EndY=96.314 EndZ=0
    g359: LineSegment StartX=286.833 StartY=96.314 StartZ=0 EndX=280.082 EndY=96.314 EndZ=0
    g360: LineSegment StartX=280.082 StartY=96.314 StartZ=0 EndX=280.082 EndY=93.0836 EndZ=0
    g361: LineSegment StartX=280.082 StartY=93.0836 StartZ=0 EndX=278.558 EndY=93.0836 EndZ=0
    g362: LineSegment StartX=278.558 StartY=93.0836 StartZ=0 EndX=278.558 EndY=97.7829 EndZ=0
    g363: LineSegment StartX=278.558 StartY=97.7829 StartZ=0 EndX=264.557 EndY=97.7829 EndZ=0
    g364: LineSegment StartX=7.38216 StartY=97.7829 StartZ=0 EndX=21.383 EndY=97.7829 EndZ=0
    g365: LineSegment StartX=21.383 StartY=97.7829 StartZ=0 EndX=21.383 EndY=83.7833 EndZ=0
    g366: LineSegment StartX=21.383 StartY=83.7833 StartZ=0 EndX=7.38216 EndY=83.7833 EndZ=0
    g367: LineSegment StartX=7.38216 StartY=83.7833 StartZ=0 EndX=7.38216 EndY=97.7829 EndZ=0
    g368: LineSegment StartX=26.4322 StartY=97.7829 StartZ=0 EndX=40.4329 EndY=97.7829 EndZ=0
    g369: LineSegment StartX=40.4329 StartY=97.7829 StartZ=0 EndX=40.4329 EndY=83.7833 EndZ=0
    g370: LineSegment StartX=40.4329 StartY=83.7833 StartZ=0 EndX=26.4322 EndY=83.7833 EndZ=0
    g371: LineSegment StartX=26.4322 StartY=83.7833 StartZ=0 EndX=26.4322 EndY=97.7829 EndZ=0
    g372: LineSegment StartX=45.4822 StartY=97.7829 StartZ=0 EndX=59.4829 EndY=97.7829 EndZ=0
    g373: LineSegment StartX=59.4829 StartY=97.7829 StartZ=0 EndX=59.4829 EndY=83.7833 EndZ=0
    g374: LineSegment StartX=59.4829 StartY=83.7833 StartZ=0 EndX=45.4822 EndY=83.7833 EndZ=0
    g375: LineSegment StartX=45.4822 StartY=83.7833 StartZ=0 EndX=45.4822 EndY=97.7829 EndZ=0
    g376: LineSegment StartX=64.5322 StartY=97.7829 StartZ=0 EndX=78.5329 EndY=97.7829 EndZ=0
    g377: LineSegment StartX=78.5329 StartY=97.7829 StartZ=0 EndX=78.5329 EndY=83.7833 EndZ=0
    g378: LineSegment StartX=78.5329 StartY=83.7833 StartZ=0 EndX=64.5322 EndY=83.7833 EndZ=0
    g379: LineSegment StartX=64.5322 StartY=83.7833 StartZ=0 EndX=64.5322 EndY=97.7829 EndZ=0
    g380: LineSegment StartX=83.5822 StartY=97.7829 StartZ=0 EndX=97.5829 EndY=97.7829 EndZ=0
    g381: LineSegment StartX=97.5829 StartY=97.7829 StartZ=0 EndX=97.5829 EndY=83.7833 EndZ=0
    g382: LineSegment StartX=97.5829 StartY=83.7833 StartZ=0 EndX=83.5822 EndY=83.7833 EndZ=0
    g383: LineSegment StartX=83.5822 StartY=83.7833 StartZ=0 EndX=83.5822 EndY=97.7829 EndZ=0
    g384: LineSegment StartX=102.632 StartY=97.7829 StartZ=0 EndX=116.633 EndY=97.7829 EndZ=0
    g385: LineSegment StartX=116.633 StartY=97.7829 StartZ=0 EndX=116.633 EndY=83.7833 EndZ=0
    g386: LineSegment StartX=116.633 StartY=83.7833 StartZ=0 EndX=102.632 EndY=83.7833 EndZ=0
    g387: LineSegment StartX=102.632 StartY=83.7833 StartZ=0 EndX=102.632 EndY=97.7829 EndZ=0
    g388: LineSegment StartX=121.682 StartY=97.7829 StartZ=0 EndX=135.683 EndY=97.7829 EndZ=0
    g389: LineSegment StartX=135.683 StartY=97.7829 StartZ=0 EndX=135.683 EndY=83.7833 EndZ=0
    g390: LineSegment StartX=135.683 StartY=83.7833 StartZ=0 EndX=121.682 EndY=83.7833 EndZ=0
    g391: LineSegment StartX=121.682 StartY=83.7833 StartZ=0 EndX=121.682 EndY=97.7829 EndZ=0
    g392: LineSegment StartX=140.732 StartY=97.7829 StartZ=0 EndX=154.733 EndY=97.7829 EndZ=0
    g393: LineSegment StartX=154.733 StartY=97.7829 StartZ=0 EndX=154.733 EndY=83.7833 EndZ=0
    g394: LineSegment StartX=154.733 StartY=83.7833 StartZ=0 EndX=140.732 EndY=83.7833 EndZ=0
    g395: LineSegment StartX=140.732 StartY=83.7833 StartZ=0 EndX=140.732 EndY=97.7829 EndZ=0
    g396: LineSegment StartX=159.782 StartY=97.7829 StartZ=0 EndX=173.783 EndY=97.7829 EndZ=0
    g397: LineSegment StartX=173.783 StartY=97.7829 StartZ=0 EndX=173.783 EndY=83.7833 EndZ=0
    g398: LineSegment StartX=173.783 StartY=83.7833 StartZ=0 EndX=159.782 EndY=83.7833 EndZ=0
    g399: LineSegment StartX=159.782 StartY=83.7833 StartZ=0 EndX=159.782 EndY=97.7829 EndZ=0
    ... +84 more geometry lines
  constraints (968):
    c: Horizontal(g0)
    c: Coincident(g0,g1)
    c: Vertical(g1)
    c: Coincident(g1,g2)
    c: Horizontal(g2)
    c: Coincident(g2,g3)
    c: Vertical(g3)
    c: Coincident(g3,g0)
    c: Horizontal(g4)
    c: Coincident(g4,g5)
    c: Vertical(g5)
    c: Coincident(g5,g6)
    c: Horizontal(g6)
    c: Coincident(g6,g7)
    c: Vertical(g7)
    c: Coincident(g7,g4)
    c: Horizontal(g8)
    c: Coincident(g8,g9)
    c: Vertical(g9)
    c: Coincident(g9,g10)
    c: Horizontal(g10)
    c: Coincident(g10,g11)
    c: Vertical(g11)
    c: Coincident(g11,g8)
    c: Vertical(g12)
    c: Coincident(g12,g13)
    c: Horizontal(g13)
    c: Coincident(g13,g14)
    c: Vertical(g14)
    c: Coincident(g14,g15)
    c: Horizontal(g15)
    c: Coincident(g15,g16)
    c: Vertical(g16)
    c: Coincident(g16,g17)
    c: Horizontal(g17)
    c: Coincident(g17,g18)
    c: Vertical(g18)
    c: Coincident(g18,g19)
    c: Horizontal(g19)
    c: Coincident(g19,g20)
    c: Vertical(g20)
    c: Coincident(g20,g21)
    c: Horizontal(g21)
    c: Coincident(g21,g22)
    c: Vertical(g22)
    c: Coincident(g22,g23)
    c: Horizontal(g23)
    c: Coincident(g23,g24)
    c: Vertical(g24)
    c: Coincident(g24,g25)
    c: Horizontal(g25)
    c: Coincident(g25,g26)
    c: Vertical(g26)
    c: Coincident(g26,g27)
    c: Horizontal(g27)
    c: Coincident(g27,g28)
    c: Vertical(g28)
    c: Coincident(g28,g29)
    c: Horizontal(g29)
    c: Coincident(g29,g30)
    c: Vertical(g30)
    c: Coincident(g30,g31)
    c: Horizontal(g31)
    c: Coincident(g31,g32)
    c: Vertical(g32)
    c: Coincident(g32,g33)
    c: Horizontal(g33)
    c: Coincident(g33,g34)
    c: Vertical(g34)
    c: Coincident(g34,g35)
    c: Horizontal(g35)
    c: Coincident(g35,g36)
    c: Vertical(g36)
    c: Coincident(g36,g37)
    c: Horizontal(g37)
    c: Coincident(g37,g38)
    c: Vertical(g38)
    c: Coincident(g38,g39)
    c: Horizontal(g39)
    c: Coincident(g39,g40)
    c: Vertical(g40)
    c: Coincident(g40,g41)
    c: Horizontal(g41)
    c: Coincident(g41,g42)
    c: Vertical(g42)
    c: Coincident(g42,g43)
    c: Horizontal(g43)
    c: Coincident(g43,g44)
    c: Vertical(g44)
    c: Coincident(g44,g45)
    c: Horizontal(g45)
    c: Coincident(g45,g46)
    c: Vertical(g46)
    c: Coincident(g46,g47)
    c: Horizontal(g47)
    c: Coincident(g47,g12)
    c: Horizontal(g48)
    c: Coincident(g48,g49)
    c: Vertical(g49)
    c: Coincident(g49,g50)
    c: Horizontal(g50)
    c: Coincident(g50,g51)
    c: Vertical(g51)
    c: Coincident(g51,g48)
    c: Horizontal(g52)
    c: Coincident(g52,g53)
    c: Vertical(g53)
    c: Coincident(g53,g54)
    c: Horizontal(g54)
    c: Coincident(g54,g55)
    c: Vertical(g55)
    c: Coincident(g55,g52)
    c: Horizontal(g56)
    c: Coincident(g56,g57)
    c: Vertical(g57)
    c: Coincident(g57,g58)
    c: Horizontal(g58)
    c: Coincident(g58,g59)
    c: Vertical(g59)
    c: Coincident(g59,g56)
    c: Horizontal(g60)
    c: Coincident(g60,g61)
    c: Vertical(g61)
    c: Coincident(g61,g62)
    c: Horizontal(g62)
    c: Coincident(g62,g63)
    c: Vertical(g63)
    c: Coincident(g63,g60)
    c: Horizontal(g64)
    c: Coincident(g64,g65)
    c: Vertical(g65)
    c: Coincident(g65,g66)
    c: Horizontal(g66)
    c: Coincident(g66,g67)
    c: Vertical(g67)
    c: Coincident(g67,g64)
    c: Horizontal(g68)
    c: Coincident(g68,g69)
    c: Vertical(g69)
    c: Coincident(g69,g70)
    c: Horizontal(g70)
    c: Coincident(g70,g71)
    c: Vertical(g71)
    c: Coincident(g71,g68)
    c: Horizontal(g72)
    c: Coincident(g72,g73)
    c: Vertical(g73)
    c: Coincident(g73,g74)
    c: Horizontal(g74)
    c: Coincident(g74,g75)
    c: Vertical(g75)
    c: Coincident(g75,g72)
    c: Horizontal(g76)
    c: Coincident(g76,g77)
    c: Vertical(g77)
    c: Coincident(g77,g78)
    c: Horizontal(g78)
    c: Coincident(g78,g79)
    c: Vertical(g79)
    c: Coincident(g79,g76)
    c: Vertical(g80)
    c: Coincident(g80,g81)
    c: Horizontal(g81)
    c: Coincident(g81,g82)
    c: Vertical(g82)
    c: Coincident(g82,g83)
    c: Horizontal(g83)
    c: Coincident(g83,g84)
    c: Vertical(g84)
    c: Coincident(g84,g85)
    c: Horizontal(g85)
    c: Coincident(g85,g86)
    c: Vertical(g86)
    c: Coincident(g86,g87)
    c: Horizontal(g87)
    c: Coincident(g87,g88)
    c: Vertical(g88)
    c: Coincident(g88,g89)
    c: Horizontal(g89)
    c: Coincident(g89,g90)
    c: Vertical(g90)
    c: Coincident(g90,g91)
    c: Horizontal(g91)
    c: Coincident(g91,g92)
    c: Vertical(g92)
    c: Coincident(g92,g93)
    c: Horizontal(g93)
    c: Coincident(g93,g94)
    c: Vertical(g94)
    c: Coincident(g94,g95)
    c: Horizontal(g95)
    c: Coincident(g95,g96)
    c: Vertical(g96)
    c: Coincident(g96,g97)
    c: Horizontal(g97)
    c: Coincident(g97,g98)
    c: Vertical(g98)
    c: Coincident(g98,g99)
    c: Horizontal(g99)
    c: Coincident(g99,g100)
    c: Vertical(g100)
    c: Coincident(g100,g101)
    c: Horizontal(g101)
    c: Coincident(g101,g102)
    c: Vertical(g102)
    c: Coincident(g102,g103)
    c: Horizontal(g103)
    c: Coincident(g103,g104)
    c: Vertical(g104)
    c: Coincident(g104,g105)
    c: Horizontal(g105)
    c: Coincident(g105,g106)
    c: Vertical(g106)
    c: Coincident(g106,g107)
    c: Horizontal(g107)
    c: Coincident(g107,g108)
    c: Vertical(g108)
    c: Coincident(g108,g109)
    c: Horizontal(g109)
    c: Coincident(g109,g110)
    c: Vertical(g110)
    c: Coincident(g110,g111)
    c: Horizontal(g111)
    c: Coincident(g111,g112)
    c: Vertical(g112)
    c: Coincident(g112,g113)
    c: Horizontal(g113)
    c: Coincident(g113,g114)
    c: Vertical(g114)
    c: Coincident(g114,g115)
    c: Horizontal(g115)
    c: Coincident(g115,g80)
    c: Vertical(g116)
    c: Coincident(g116,g117)
    c: Horizontal(g117)
    c: Coincident(g117,g118)
    c: Vertical(g118)
    c: Coincident(g118,g119)
    c: Horizontal(g119)
    c: Coincident(g119,g120)
    c: Vertical(g120)
    c: Coincident(g120,g121)
    c: Horizontal(g121)
    c: Coincident(g121,g122)
    c: Vertical(g122)
    c: Coincident(g122,g123)
    c: Horizontal(g123)
    c: Coincident(g123,g124)
    c: Vertical(g124)
    c: Coincident(g124,g125)
    c: Horizontal(g125)
    c: Coincident(g125,g126)
    c: Vertical(g126)
    c: Coincident(g126,g127)
    c: Horizontal(g127)
    c: Coincident(g127,g128)
    c: Vertical(g128)
    c: Coincident(g128,g129)
    c: Horizontal(g129)
    c: Coincident(g129,g130)
    c: Vertical(g130)
    c: Coincident(g130,g131)
    c: Horizontal(g131)
    c: Coincident(g131,g132)
    c: Vertical(g132)
    c: Coincident(g132,g133)
    c: Horizontal(g133)
    c: Coincident(g133,g134)
    c: Vertical(g134)
    c: Coincident(g134,g135)
    c: Horizontal(g135)
    c: Coincident(g135,g136)
    c: Vertical(g136)
    c: Coincident(g136,g137)
    c: Horizontal(g137)
    c: Coincident(g137,g138)
    c: Vertical(g138)
    c: Coincident(g138,g139)
    c: Horizontal(g139)
    c: Coincident(g139,g140)
    c: Vertical(g140)
    c: Coincident(g140,g141)
    c: Horizontal(g141)
    c: Coincident(g141,g142)
    c: Vertical(g142)
    c: Coincident(g142,g143)
    c: Horizontal(g143)
    c: Coincident(g143,g144)
    c: Vertical(g144)
    c: Coincident(g144,g145)
    c: Horizontal(g145)
    c: Coincident(g145,g146)
    c: Vertical(g146)
    c: Coincident(g146,g147)
    c: Horizontal(g147)
    c: Coincident(g147,g148)
    c: Vertical(g148)
    c: Coincident(g148,g149)
    c: Horizontal(g149)
    c: Coincident(g149,g150)
    c: Vertical(g150)
    c: Coincident(g150,g151)
    c: Horizontal(g151)
    c: Coincident(g151,g116)
    c: Horizontal(g152)
    c: Coincident(g152,g153)
    c: Vertical(g153)
    c: Coincident(g153,g154)
    c: Horizontal(g154)
    c: Coincident(g154,g155)
    c: Vertical(g155)
    c: Coincident(g155,g152)
    c: Horizontal(g156)
    c: Coincident(g156,g157)
    c: Vertical(g157)
    c: Coincident(g157,g158)
    c: Horizontal(g158)
    c: Coincident(g158,g159)
    c: Vertical(g159)
    c: Coincident(g159,g156)
    c: Horizontal(g160)
    c: Coincident(g160,g161)
    c: Vertical(g161)
    c: Coincident(g161,g162)
    c: Horizontal(g162)
    c: Coincident(g162,g163)
    c: Vertical(g163)
    c: Coincident(g163,g160)
    c: Horizontal(g164)
    c: Coincident(g164,g165)
    c: Vertical(g165)
    c: Coincident(g165,g166)
    c: Horizontal(g166)
    c: Coincident(g166,g167)
    c: Vertical(g167)
    c: Coincident(g167,g164)
    c: Horizontal(g168)
    c: Coincident(g168,g169)
    c: Vertical(g169)
    c: Coincident(g169,g170)
    c: Horizontal(g170)
    c: Coincident(g170,g171)
    c: Vertical(g171)
    c: Coincident(g171,g168)
    c: Horizontal(g172)
    c: Coincident(g172,g173)
    c: Vertical(g173)
    c: Coincident(g173,g174)
    c: Horizontal(g174)
    c: Coincident(g174,g175)
    c: Vertical(g175)
    c: Coincident(g175,g172)
    c: Horizontal(g176)
    c: Coincident(g176,g177)
    c: Vertical(g177)
    c: Coincident(g177,g178)
    c: Horizontal(g178)
    c: Coincident(g178,g179)
    c: Vertical(g179)
    c: Coincident(g179,g176)
    c: Horizontal(g180)
    c: Coincident(g180,g181)
    c: Vertical(g181)
    c: Coincident(g181,g182)
    c: Horizontal(g182)
    c: Coincident(g182,g183)
    c: Vertical(g183)
    c: Coincident(g183,g180)
    c: Horizontal(g184)
    c: Coincident(g184,g185)
    c: Vertical(g185)
    c: Coincident(g185,g186)
    c: Horizontal(g186)
    c: Coincident(g186,g187)
    c: Vertical(g187)
    c: Coincident(g187,g184)
    c: Horizontal(g188)
    c: Coincident(g188,g189)
    c: Vertical(g189)
    c: Coincident(g189,g190)
    c: Horizontal(g190)
    c: Coincident(g190,g191)
    c: Vertical(g191)
    c: Coincident(g191,g188)
    c: Vertical(g192)
    c: Coincident(g192,g193)
    c: Horizontal(g193)
    c: Coincident(g193,g194)
    c: Vertical(g194)
    c: Coincident(g194,g195)
    c: Horizontal(g195)
    c: Coincident(g195,g196)
    c: Vertical(g196)
    c: Coincident(g196,g197)
    c: Horizontal(g197)
    c: Coincident(g197,g198)
    c: Vertical(g198)
    c: Coincident(g198,g199)
    c: Horizontal(g199)
    c: Coincident(g199,g200)
    c: Vertical(g200)
    c: Coincident(g200,g201)
    c: Horizontal(g201)
    c: Coincident(g201,g202)
    c: Vertical(g202)
    c: Coincident(g202,g203)
    c: Horizontal(g203)
    c: Coincident(g203,g204)
    c: Vertical(g204)
    c: Coincident(g204,g205)
    c: Horizontal(g205)
    c: Coincident(g205,g206)
    c: Vertical(g206)
    c: Coincident(g206,g207)
    c: Horizontal(g207)
    c: Coincident(g207,g208)
    c: Vertical(g208)
    c: Coincident(g208,g209)
    c: Horizontal(g209)
    c: Coincident(g209,g210)
    c: Vertical(g210)
    c: Coincident(g210,g211)
    c: Horizontal(g211)
    c: Coincident(g211,g212)
    c: Vertical(g212)
    c: Coincident(g212,g213)
    c: Horizontal(g213)
    c: Coincident(g213,g214)
    c: Vertical(g214)
    c: Coincident(g214,g215)
    c: Horizontal(g215)
    c: Coincident(g215,g216)
    c: Vertical(g216)
    c: Coincident(g216,g217)
    c: Horizontal(g217)
    c: Coincident(g217,g218)
    c: Vertical(g218)
    c: Coincident(g218,g219)
    c: Horizontal(g219)
    c: Coincident(g219,g220)
    c: Vertical(g220)
    c: Coincident(g220,g221)
    c: Horizontal(g221)
    c: Coincident(g221,g222)
    c: Vertical(g222)
    c: Coincident(g222,g223)
    c: Horizontal(g223)
    c: Coincident(g223,g224)
    c: Vertical(g224)
    c: Coincident(g224,g225)
    c: Horizontal(g225)
    c: Coincident(g225,g226)
    c: Vertical(g226)
    c: Coincident(g226,g227)
    c: Horizontal(g227)
    c: Coincident(g227,g192)
    c: Horizontal(g228)
    c: Coincident(g228,g229)
    c: Vertical(g229)
    c: Coincident(g229,g230)
    c: Horizontal(g230)
    c: Coincident(g230,g231)
    c: Vertical(g231)
    c: Coincident(g231,g228)
    c: Horizontal(g232)
    c: Coincident(g232,g233)
    c: Vertical(g233)
    c: Coincident(g233,g234)
    c: Horizontal(g234)
    c: Coincident(g234,g235)
    c: Vertical(g235)
    c: Coincident(g235,g232)
    c: Horizontal(g236)
    c: Coincident(g236,g237)
    c: Vertical(g237)
    c: Coincident(g237,g238)
    c: Horizontal(g238)
    c: Coincident(g238,g239)
    c: Vertical(g239)
    c: Coincident(g239,g236)
    c: Horizontal(g240)
    c: Coincident(g240,g241)
    c: Vertical(g241)
    c: Coincident(g241,g242)
    c: Horizontal(g242)
    c: Coincident(g242,g243)
    c: Vertical(g243)
    c: Coincident(g243,g240)
    c: Horizontal(g244)
    c: Coincident(g244,g245)
    c: Vertical(g245)
    c: Coincident(g245,g246)
    c: Horizontal(g246)
    c: Coincident(g246,g247)
    c: Vertical(g247)
    c: Coincident(g247,g244)
    c: Horizontal(g248)
    c: Coincident(g248,g249)
    c: Vertical(g249)
    c: Coincident(g249,g250)
    c: Horizontal(g250)
    c: Coincident(g250,g251)
    c: Vertical(g251)
    c: Coincident(g251,g248)
    c: Horizontal(g252)
    c: Coincident(g252,g253)
    c: Vertical(g253)
    c: Coincident(g253,g254)
    c: Horizontal(g254)
    c: Coincident(g254,g255)
    c: Vertical(g255)
    c: Coincident(g255,g252)
    c: Horizontal(g256)
    c: Coincident(g256,g257)
    c: Vertical(g257)
    c: Coincident(g257,g258)
    c: Horizontal(g258)
    c: Coincident(g258,g259)
    c: Vertical(g259)
    c: Coincident(g259,g256)
    c: Horizontal(g260)
    c: Coincident(g260,g261)
    c: Vertical(g261)
    c: Coincident(g261,g262)
    c: Horizontal(g262)
    c: Coincident(g262,g263)
    c: Vertical(g263)
    c: Coincident(g263,g260)
    c: Horizontal(g264)
    c: Coincident(g264,g265)
    c: Vertical(g265)
    c: Coincident(g265,g266)
    c: Horizontal(g266)
    c: Coincident(g266,g267)
    c: Vertical(g267)
    c: Coincident(g267,g264)
    c: Horizontal(g268)
    c: Coincident(g268,g269)
    c: Vertical(g269)
    c: Coincident(g269,g270)
    c: Horizontal(g270)
    c: Coincident(g270,g271)
    c: Vertical(g271)
    c: Coincident(g271,g268)
    c: Horizontal(g272)
    c: Coincident(g272,g273)
    c: Vertical(g273)
    c: Coincident(g273,g274)
    c: Horizontal(g274)
    c: Coincident(g274,g275)
    c: Vertical(g275)
    c: Coincident(g275,g272)
    c: Horizontal(g276)
    c: Coincident(g276,g277)
    c: Vertical(g277)
    c: Coincident(g277,g278)
    c: Horizontal(g278)
    c: Coincident(g278,g279)
    c: Vertical(g279)
    c: Coincident(g279,g276)
    c: Horizontal(g280)
    c: Coincident(g280,g281)
    c: Vertical(g281)
    c: Coincident(g281,g282)
    c: Horizontal(g282)
    c: Coincident(g282,g283)
    c: Vertical(g283)
    c: Coincident(g283,g280)
    c: Horizontal(g284)
    c: Coincident(g284,g285)
    c: Vertical(g285)
    c: Coincident(g285,g286)
    c: Horizontal(g286)
    c: Coincident(g286,g287)
    c: Vertical(g287)
    c: Coincident(g287,g284)
    c: Horizontal(g288)
    c: Coincident(g288,g289)
    c: Vertical(g289)
    c: Coincident(g289,g290)
    c: Horizontal(g290)
    c: Coincident(g290,g291)
    c: Vertical(g291)
    c: Coincident(g291,g288)
    c: Horizontal(g292)
    c: Coincident(g292,g293)
    c: Vertical(g293)
    c: Coincident(g293,g294)
    c: Horizontal(g294)
    c: Coincident(g294,g295)
    c: Vertical(g295)
    c: Coincident(g295,g292)
    c: Horizontal(g296)
    c: Coincident(g296,g297)
    c: Vertical(g297)
    c: Coincident(g297,g298)
    c: Horizontal(g298)
    c: Coincident(g298,g299)
    c: Vertical(g299)
    c: Coincident(g299,g296)
    c: Horizontal(g300)
    c: Coincident(g300,g301)
    c: Vertical(g301)
    c: Coincident(g301,g302)
    c: Horizontal(g302)
    c: Coincident(g302,g303)
    c: Vertical(g303)
    c: Coincident(g303,g300)
    c: Horizontal(g304)
    c: Coincident(g304,g305)
    c: Vertical(g305)
    c: Coincident(g305,g306)
    c: Horizontal(g306)
    c: Coincident(g306,g307)
    c: Vertical(g307)
    c: Coincident(g307,g304)
    c: Horizontal(g308)
    c: Coincident(g308,g309)
    c: Vertical(g309)
    c: Coincident(g309,g310)
    c: Horizontal(g310)
    c: Coincident(g310,g311)
    c: Vertical(g311)
    c: Coincident(g311,g308)
    c: Horizontal(g312)
    c: Coincident(g312,g313)
    c: Vertical(g313)
    c: Coincident(g313,g314)
    c: Horizontal(g314)
    c: Coincident(g314,g315)
    c: Vertical(g315)
    c: Coincident(g315,g312)
    c: Horizontal(g316)
    c: Coincident(g316,g317)
    c: Vertical(g317)
    c: Coincident(g317,g318)
    c: Horizontal(g318)
    c: Coincident(g318,g319)
    c: Vertical(g319)
    c: Coincident(g319,g316)
    c: Horizontal(g320)
    c: Coincident(g320,g321)
    c: Vertical(g321)
    c: Coincident(g321,g322)
    c: Horizontal(g322)
    c: Coincident(g322,g323)
    c: Vertical(g323)
    c: Coincident(g323,g320)
    c: Horizontal(g324)
    c: Coincident(g324,g325)
    c: Vertical(g325)
    c: Coincident(g325,g326)
    c: Horizontal(g326)
    c: Coincident(g326,g327)
    c: Vertical(g327)
    c: Coincident(g327,g324)
    c: Vertical(g328)
    c: Coincident(g328,g329)
    c: Horizontal(g329)
    c: Coincident(g329,g330)
    c: Vertical(g330)
    c: Coincident(g330,g331)
    c: Horizontal(g331)
    c: Coincident(g331,g332)
    c: Vertical(g332)
    c: Coincident(g332,g333)
    c: Horizontal(g333)
    c: Coincident(g333,g334)
    c: Vertical(g334)
    c: Coincident(g334,g335)
    c: Horizontal(g335)
    c: Coincident(g335,g336)
    c: Vertical(g336)
    c: Coincident(g336,g337)
    c: Horizontal(g337)
    c: Coincident(g337,g338)
    c: Vertical(g338)
    c: Coincident(g338,g339)
    c: Horizontal(g339)
    c: Coincident(g339,g340)
    c: Vertical(g340)
    c: Coincident(g340,g341)
    c: Horizontal(g341)
    c: Coincident(g341,g342)
    c: Vertical(g342)
    c: Coincident(g342,g343)
    c: Horizontal(g343)
    c: Coincident(g343,g344)
    c: Vertical(g344)
    c: Coincident(g344,g345)
    c: Horizontal(g345)
    c: Coincident(g345,g346)
    c: Vertical(g346)
    c: Coincident(g346,g347)
    c: Horizontal(g347)
    c: Coincident(g347,g348)
    c: Vertical(g348)
    c: Coincident(g348,g349)
    c: Horizontal(g349)
    c: Coincident(g349,g350)
    c: Vertical(g350)
    c: Coincident(g350,g351)
    c: Horizontal(g351)
    c: Coincident(g351,g352)
    c: Vertical(g352)
    c: Coincident(g352,g353)
    c: Horizontal(g353)
    c: Coincident(g353,g354)
    c: Vertical(g354)
    c: Coincident(g354,g355)
    c: Horizontal(g355)
    c: Coincident(g355,g356)
    c: Vertical(g356)
    c: Coincident(g356,g357)
    c: Horizontal(g357)
    c: Coincident(g357,g358)
    c: Vertical(g358)
    c: Coincident(g358,g359)
    c: Horizontal(g359)
    c: Coincident(g359,g360)
    c: Vertical(g360)
    c: Coincident(g360,g361)
    c: Horizontal(g361)
    c: Coincident(g361,g362)
    c: Vertical(g362)
    c: Coincident(g362,g363)
    c: Horizontal(g363)
    c: Coincident(g363,g328)
    c: Horizontal(g364)
    c: Coincident(g364,g365)
    c: Vertical(g365)
    c: Coincident(g365,g366)
    c: Horizontal(g366)
    c: Coincident(g366,g367)
    c: Vertical(g367)
    c: Coincident(g367,g364)
    c: Horizontal(g368)
    c: Coincident(g368,g369)
    c: Vertical(g369)
    c: Coincident(g369,g370)
    c: Horizontal(g370)
    c: Coincident(g370,g371)
    c: Vertical(g371)
    c: Coincident(g371,g368)
    c: Horizontal(g372)
    c: Coincident(g372,g373)
    c: Vertical(g373)
    c: Coincident(g373,g374)
    c: Horizontal(g374)
    c: Coincident(g374,g375)
    c: Vertical(g375)
    c: Coincident(g375,g372)
    c: Horizontal(g376)
    c: Coincident(g376,g377)
    c: Vertical(g377)
    c: Coincident(g377,g378)
    c: Horizontal(g378)
    c: Coincident(g378,g379)
    c: Vertical(g379)
    c: Coincident(g379,g376)
    c: Horizontal(g380)
    c: Coincident(g380,g381)
    c: Vertical(g381)
    c: Coincident(g381,g382)
    c: Horizontal(g382)
    c: Coincident(g382,g383)
    c: Vertical(g383)
    c: Coincident(g383,g380)
    c: Horizontal(g384)
    c: Coincident(g384,g385)
    c: Vertical(g385)
    c: Coincident(g385,g386)
    c: Horizontal(g386)
    c: Coincident(g386,g387)
    c: Vertical(g387)
    c: Coincident(g387,g384)
    c: Horizontal(g388)
    c: Coincident(g388,g389)
    c: Vertical(g389)
    c: Coincident(g389,g390)
    c: Horizontal(g390)
    c: Coincident(g390,g391)
    c: Vertical(g391)
    c: Coincident(g391,g388)
    c: Horizontal(g392)
    c: Coincident(g392,g393)
    c: Vertical(g393)
    c: Coincident(g393,g394)
    c: Horizontal(g394)
    c: Coincident(g394,g395)
    c: Vertical(g395)
    c: Coincident(g395,g392)
    c: Horizontal(g396)
    c: Coincident(g396,g397)
    c: Vertical(g397)
    c: Coincident(g397,g398)
    c: Horizontal(g398)
    c: Coincident(g398,g399)
    c: Vertical(g399)
    c: Coincident(g399,g396)
    c: Horizontal(g400)
    c: Coincident(g400,g401)
    c: Vertical(g401)
    c: Coincident(g401,g402)
    c: Horizontal(g402)
    c: Coincident(g402,g403)
    c: Vertical(g403)
    c: Coincident(g403,g400)
    c: Horizontal(g404)
    c: Coincident(g404,g405)
    c: Vertical(g405)
    c: Coincident(g405,g406)
    c: Horizontal(g406)
    c: Coincident(g406,g407)
    c: Vertical(g407)
    c: Coincident(g407,g404)
    c: Horizontal(g408)
    c: Coincident(g408,g409)
    c: Vertical(g409)
    c: Coincident(g409,g410)
    c: Horizontal(g410)
    c: Coincident(g410,g411)
    c: Vertical(g411)
    c: Coincident(g411,g408)
    c: Horizontal(g412)
    c: Coincident(g412,g413)
    c: Vertical(g413)
    c: Coincident(g413,g414)
    c: Horizontal(g414)
    c: Coincident(g414,g415)
    c: Vertical(g415)
    c: Coincident(g415,g412)
    c: Horizontal(g416)
    c: Coincident(g416,g417)
    c: Vertical(g417)
    c: Coincident(g417,g418)
    c: Horizontal(g418)
    c: Coincident(g418,g419)
    c: Vertical(g419)
    c: Coincident(g419,g416)
    c: Horizontal(g420)
    c: Coincident(g420,g421)
    c: Vertical(g421)
    c: Coincident(g421,g422)
    c: Horizontal(g422)
    c: Coincident(g422,g423)
    c: Vertical(g423)
    c: Coincident(g423,g420)
    c: Horizontal(g424)
    c: Coincident(g424,g425)
    c: Vertical(g425)
    c: Coincident(g425,g426)
    c: Horizontal(g426)
    c: Coincident(g426,g427)
    c: Vertical(g427)
    c: Coincident(g427,g424)
    c: Horizontal(g428)
    c: Coincident(g428,g429)
    c: Vertical(g429)
    c: Coincident(g429,g430)
    c: Horizontal(g430)
    c: Coincident(g430,g431)
    c: Vertical(g431)
    c: Coincident(g431,g428)
    c: Horizontal(g432)
    c: Coincident(g432,g433)
    c: Vertical(g433)
    c: Coincident(g433,g434)
    c: Horizontal(g434)
    c: Coincident(g434,g435)
    c: Vertical(g435)
    c: Coincident(g435,g432)
    c: Horizontal(g436)
    c: Coincident(g436,g437)
    c: Vertical(g437)
    c: Coincident(g437,g438)
    c: Horizontal(g438)
    c: Coincident(g438,g439)
    c: Vertical(g439)
    c: Coincident(g439,g436)
    c: Horizontal(g440)
    c: Coincident(g440,g441)
    c: Vertical(g441)
    c: Coincident(g441,g442)
    c: Horizontal(g442)
    c: Coincident(g442,g443)
    c: Vertical(g443)
    c: Coincident(g443,g440)
    c: Horizontal(g444)
    c: Coincident(g444,g445)
    c: Vertical(g445)
    c: Coincident(g445,g446)
    c: Horizontal(g446)
    c: Coincident(g446,g447)
    c: Vertical(g447)
    c: Coincident(g447,g444)
    c: Horizontal(g448)
    c: Coincident(g448,g449)
    c: Vertical(g449)
    c: Coincident(g449,g450)
    c: Horizontal(g450)
    c: Coincident(g450,g451)
    c: Vertical(g451)
    c: Coincident(g451,g448)
    c: Horizontal(g452)
    c: Coincident(g452,g453)
    c: Vertical(g453)
    c: Coincident(g453,g454)
    c: Horizontal(g454)
    c: Coincident(g454,g455)
    c: Vertical(g455)
    c: Coincident(g455,g452)
    c: Horizontal(g456)
    c: Coincident(g456,g457)
    c: Vertical(g457)
    c: Coincident(g457,g458)
    c: Horizontal(g458)
    c: Coincident(g458,g459)
    c: Vertical(g459)
    c: Coincident(g459,g456)
    c: Horizontal(g460)
    c: Coincident(g460,g461)
    c: Vertical(g461)
    c: Coincident(g461,g462)
    c: Horizontal(g462)
    c: Coincident(g462,g463)
    c: Vertical(g463)
    c: Coincident(g463,g460)
    c: Horizontal(g464)
    c: Coincident(g464,g465)
    c: Vertical(g465)
    c: Coincident(g465,g466)
    c: Horizontal(g466)
    c: Coincident(g466,g467)
    c: Vertical(g467)
    c: Coincident(g467,g464)
    c: Horizontal(g468)
    c: Coincident(g468,g469)
    c: Vertical(g469)
    c: Coincident(g469,g470)
    c: Horizontal(g470)
    c: Coincident(g470,g471)
    c: Vertical(g471)
    c: Coincident(g471,g468)
    c: Horizontal(g472)
    c: Coincident(g472,g473)
    c: Vertical(g473)
    c: Coincident(g473,g474)
    c: Horizontal(g474)
    c: Coincident(g474,g475)
    c: Vertical(g475)
    c: Coincident(g475,g472)
    c: Horizontal(g476)
    c: Coincident(g476,g477)
    c: Vertical(g477)
    c: Coincident(g477,g478)
    c: Horizontal(g478)
    c: Coincident(g478,g479)
    c: Vertical(g479)
    c: Coincident(g479,g476)
    c: Horizontal(g480)
    c: Coincident(g480,g481)
    c: Vertical(g481)
    c: Coincident(g481,g482)
    c: Horizontal(g482)
    c: Coincident(g482,g483)
    c: Vertical(g483)
    c: Coincident(g483,g480)
FEATURE [PartDesign::Pad] Pad
  Direction = (0,0,1)
  Length = 1.5
  Length2 = 10
  Profile = -> Sketch
  ReferenceAxis = -> Sketch [N_Axis]
  Type = 0
FEATURE [PartDesign::Body] Body  label="Plate"
  Group = -> [Sketch,Pad]
  Origin = -> Origin
  Tip = -> Pad
FEATURE [PartDesign::Body] Body001  label="Body"
  Origin = -> Origin001
